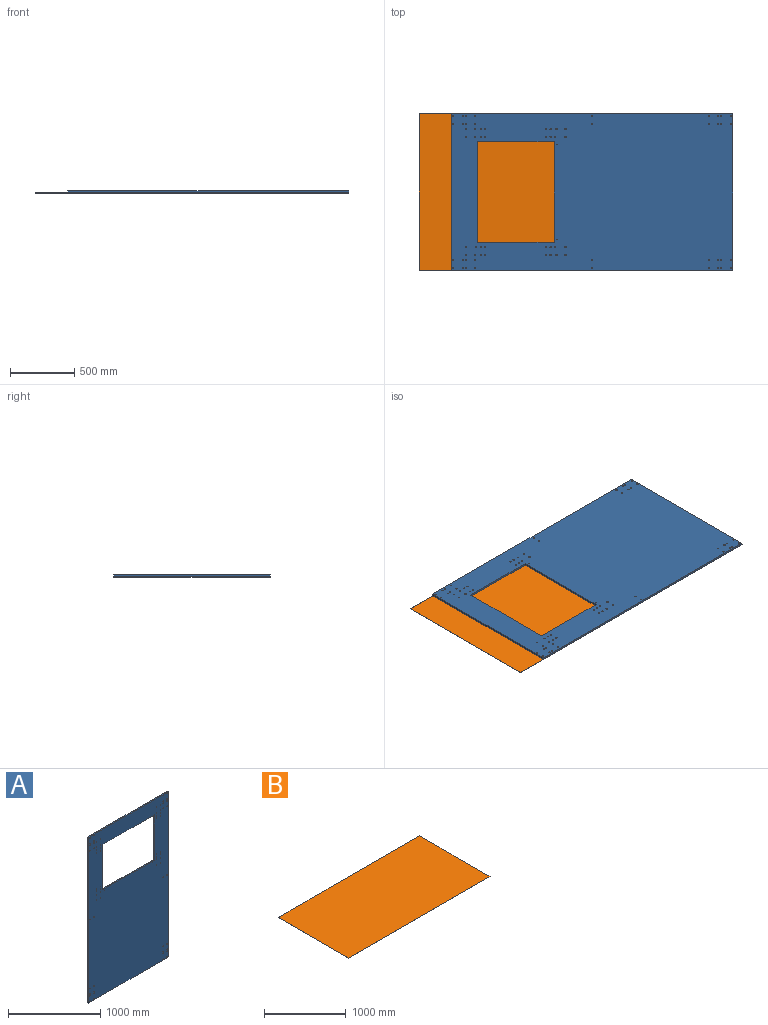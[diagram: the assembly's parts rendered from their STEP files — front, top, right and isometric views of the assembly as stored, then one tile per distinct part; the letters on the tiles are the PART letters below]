
ASSEMBLY  parts=2 mates=1
PART A: 80 faces, bbox 1220x15x2190 mm
  f0: plane 1220x15mm, normal (0,0,-1), area 18300mm2, adj f1,f77,f78,f79
  f1: plane 2190x15mm, normal (1,0,0), area 32850mm2, adj f0,f2,f78,f79
  f2: plane 1220x15mm, normal (0,0,1), area 18300mm2, adj f1,f77,f78,f79
  f3: plane 600x15mm, normal (-1,0,0), area 9000mm2, adj f4,f76,f78,f79
  f4: plane 782x15mm, normal (0,0,1), area 11730mm2, adj f3,f5,f78,f79
  f5: plane 600x15mm, normal (1,0,0), area 9000mm2, adj f4,f76,f78,f79
  f6: cylinder r=5mm len=15mm, axis (0,1,0), area 471.2mm2, adj f78,f79
  f7: cylinder r=5mm len=15mm, axis (0,1,0), area 471.2mm2, adj f78,f79
  f8: cylinder r=5mm len=15mm, axis (0,1,0), area 471.2mm2, adj f78,f79
  f9: cylinder r=5mm len=15mm, axis (0,1,0), area 471.2mm2, adj f78,f79
  f10: cylinder r=5mm len=15mm, axis (0,1,0), area 471.2mm2, adj f78,f79
  f11: cylinder r=5mm len=15mm, axis (0,1,0), area 471.2mm2, adj f78,f79
  f12: cylinder r=5mm len=15mm, axis (0,1,0), area 471.2mm2, adj f78,f79
  f13: cylinder r=5mm len=15mm, axis (0,1,0), area 471.2mm2, adj f78,f79
  f14: cylinder r=5mm len=15mm, axis (0,1,0), area 471.2mm2, adj f78,f79
  f15: cylinder r=5mm len=15mm, axis (0,1,0), area 471.2mm2, adj f78,f79
  f16: cylinder r=3mm len=15mm, axis (0,1,0), area 282.7mm2, adj f78,f79
  f17: cylinder r=5mm len=15mm, axis (0,1,0), area 471.2mm2, adj f78,f79
  f18: cylinder r=5mm len=15mm, axis (0,1,0), area 471.2mm2, adj f78,f79
  f19: cylinder r=5mm len=15mm, axis (0,1,0), area 471.2mm2, adj f78,f79
  f20: cylinder r=5mm len=15mm, axis (0,1,0), area 471.2mm2, adj f78,f79
  f21: cylinder r=5mm len=15mm, axis (0,1,0), area 471.2mm2, adj f78,f79
  f22: cylinder r=5mm len=15mm, axis (0,1,0), area 471.2mm2, adj f78,f79
  f23: cylinder r=5mm len=15mm, axis (0,1,0), area 471.2mm2, adj f78,f79
  f24: cylinder r=5mm len=15mm, axis (0,1,0), area 471.2mm2, adj f78,f79
  f25: cylinder r=5mm len=15mm, axis (0,1,0), area 471.2mm2, adj f78,f79
  f26: cylinder r=5mm len=15mm, axis (0,1,0), area 471.2mm2, adj f78,f79
  f27: cylinder r=5mm len=15mm, axis (0,1,0), area 471.2mm2, adj f78,f79
  f28: cylinder r=5mm len=15mm, axis (0,1,0), area 471.2mm2, adj f78,f79
  f29: cylinder r=5mm len=15mm, axis (0,1,0), area 471.2mm2, adj f78,f79
  f30: cylinder r=5mm len=15mm, axis (0,1,0), area 471.2mm2, adj f78,f79
  f31: cylinder r=5mm len=15mm, axis (0,1,0), area 471.2mm2, adj f78,f79
  f32: cylinder r=5mm len=15mm, axis (0,1,0), area 471.2mm2, adj f78,f79
  f33: cylinder r=5mm len=15mm, axis (0,1,0), area 471.2mm2, adj f78,f79
  f34: cylinder r=5mm len=15mm, axis (0,1,0), area 471.2mm2, adj f78,f79
  f35: cylinder r=5mm len=15mm, axis (0,1,0), area 471.2mm2, adj f78,f79
  f36: cylinder r=5mm len=15mm, axis (0,1,0), area 471.2mm2, adj f78,f79
  f37: cylinder r=5mm len=15mm, axis (0,1,0), area 471.2mm2, adj f78,f79
  f38: cylinder r=5mm len=15mm, axis (0,1,0), area 471.2mm2, adj f78,f79
  f39: cylinder r=5mm len=15mm, axis (0,1,0), area 471.2mm2, adj f78,f79
  f40: cylinder r=5mm len=15mm, axis (0,1,0), area 471.2mm2, adj f78,f79
  f41: cylinder r=5mm len=15mm, axis (0,1,0), area 471.2mm2, adj f78,f79
  f42: cylinder r=5mm len=15mm, axis (0,1,0), area 471.2mm2, adj f78,f79
  f43: cylinder r=5mm len=15mm, axis (0,1,0), area 471.2mm2, adj f78,f79
  f44: cylinder r=5mm len=15mm, axis (0,1,0), area 471.2mm2, adj f78,f79
  f45: cylinder r=5mm len=15mm, axis (0,1,0), area 471.2mm2, adj f78,f79
  f46: cylinder r=5mm len=15mm, axis (0,1,0), area 471.2mm2, adj f78,f79
  f47: cylinder r=5mm len=15mm, axis (0,1,0), area 471.2mm2, adj f78,f79
  f48: cylinder r=5mm len=15mm, axis (0,1,0), area 471.2mm2, adj f78,f79
  f49: cylinder r=3mm len=15mm, axis (0,1,0), area 282.7mm2, adj f78,f79
  f50: cylinder r=5mm len=15mm, axis (0,1,0), area 471.2mm2, adj f78,f79
  f51: cylinder r=5mm len=15mm, axis (0,1,0), area 471.2mm2, adj f78,f79
  f52: cylinder r=5mm len=15mm, axis (0,1,0), area 471.2mm2, adj f78,f79
  f53: cylinder r=5mm len=15mm, axis (0,1,0), area 471.2mm2, adj f78,f79
  f54: cylinder r=5mm len=15mm, axis (0,1,0), area 471.2mm2, adj f78,f79
  f55: cylinder r=5mm len=15mm, axis (0,1,0), area 471.2mm2, adj f78,f79
  f56: cylinder r=5mm len=15mm, axis (0,1,0), area 471.2mm2, adj f78,f79
  f57: cylinder r=5mm len=15mm, axis (0,1,0), area 471.2mm2, adj f78,f79
  f58: cylinder r=5mm len=15mm, axis (0,1,0), area 471.2mm2, adj f78,f79
  f59: cylinder r=5mm len=15mm, axis (0,1,0), area 471.2mm2, adj f78,f79
  f60: cylinder r=5mm len=15mm, axis (0,1,0), area 471.2mm2, adj f78,f79
  f61: cylinder r=5mm len=15mm, axis (0,1,0), area 471.2mm2, adj f78,f79
  f62: cylinder r=5mm len=15mm, axis (0,1,0), area 471.2mm2, adj f78,f79
  f63: cylinder r=5mm len=15mm, axis (0,1,0), area 471.2mm2, adj f78,f79
  f64: cylinder r=5mm len=15mm, axis (0,1,0), area 471.2mm2, adj f78,f79
  f65: cylinder r=5mm len=15mm, axis (0,1,0), area 471.2mm2, adj f78,f79
  f66: cylinder r=5mm len=15mm, axis (0,1,0), area 471.2mm2, adj f78,f79
  f67: cylinder r=5mm len=15mm, axis (0,1,0), area 471.2mm2, adj f78,f79
  f68: cylinder r=5mm len=15mm, axis (0,1,0), area 471.2mm2, adj f78,f79
  f69: cylinder r=5mm len=15mm, axis (0,1,0), area 471.2mm2, adj f78,f79
  f70: cylinder r=5mm len=15mm, axis (0,1,0), area 471.2mm2, adj f78,f79
  f71: cylinder r=5mm len=15mm, axis (0,1,0), area 471.2mm2, adj f78,f79
  f72: cylinder r=5mm len=15mm, axis (0,1,0), area 471.2mm2, adj f78,f79
  f73: cylinder r=5mm len=15mm, axis (0,1,0), area 471.2mm2, adj f78,f79
  f74: cylinder r=5mm len=15mm, axis (0,1,0), area 471.2mm2, adj f78,f79
  f75: cylinder r=5mm len=15mm, axis (0,1,0), area 471.2mm2, adj f78,f79
  f76: plane 782x15mm, normal (0,0,-1), area 11730mm2, adj f3,f5,f78,f79
  f77: plane 2190x15mm, normal (-1,0,0), area 32850mm2, adj f0,f2,f78,f79
  f78: plane 2190x1220mm, normal (0,-1,0), area 2197201.2mm2, adj f0,f1,f2,f3,f4,f5,f6,f7
  f79: plane 2190x1220mm, normal (0,1,0), area 2197201.2mm2, adj f0,f1,f2,f3,f4,f5,f6,f7
PART B: 6 faces, bbox 2440x1220x1 mm
  f0: plane 1220x1mm, normal (-1,0,0), area 1220mm2, adj f1,f3,f4,f5
  f1: plane 2440x1mm, normal (0,-1,0), area 2440mm2, adj f0,f2,f4,f5
  f2: plane 1220x1mm, normal (1,0,0), area 1220mm2, adj f1,f3,f4,f5
  f3: plane 2440x1mm, normal (0,1,0), area 2440mm2, adj f0,f2,f4,f5
  f4: plane 2440x1220mm, normal (0,0,1), area 2976800mm2, adj f0,f1,f2,f3
  f5: plane 2440x1220mm, normal (0,0,-1), area 2976800mm2, adj f0,f1,f2,f3
PLACE A rot(axis=(0.58,-0.58,-0.58),120deg) t=(125,-9,8.5)mm
PLACE B at identity fixed
MATE fastened A.f78 <-> B.f4  axis (0,0,-1) through (1220,610,1)mm
